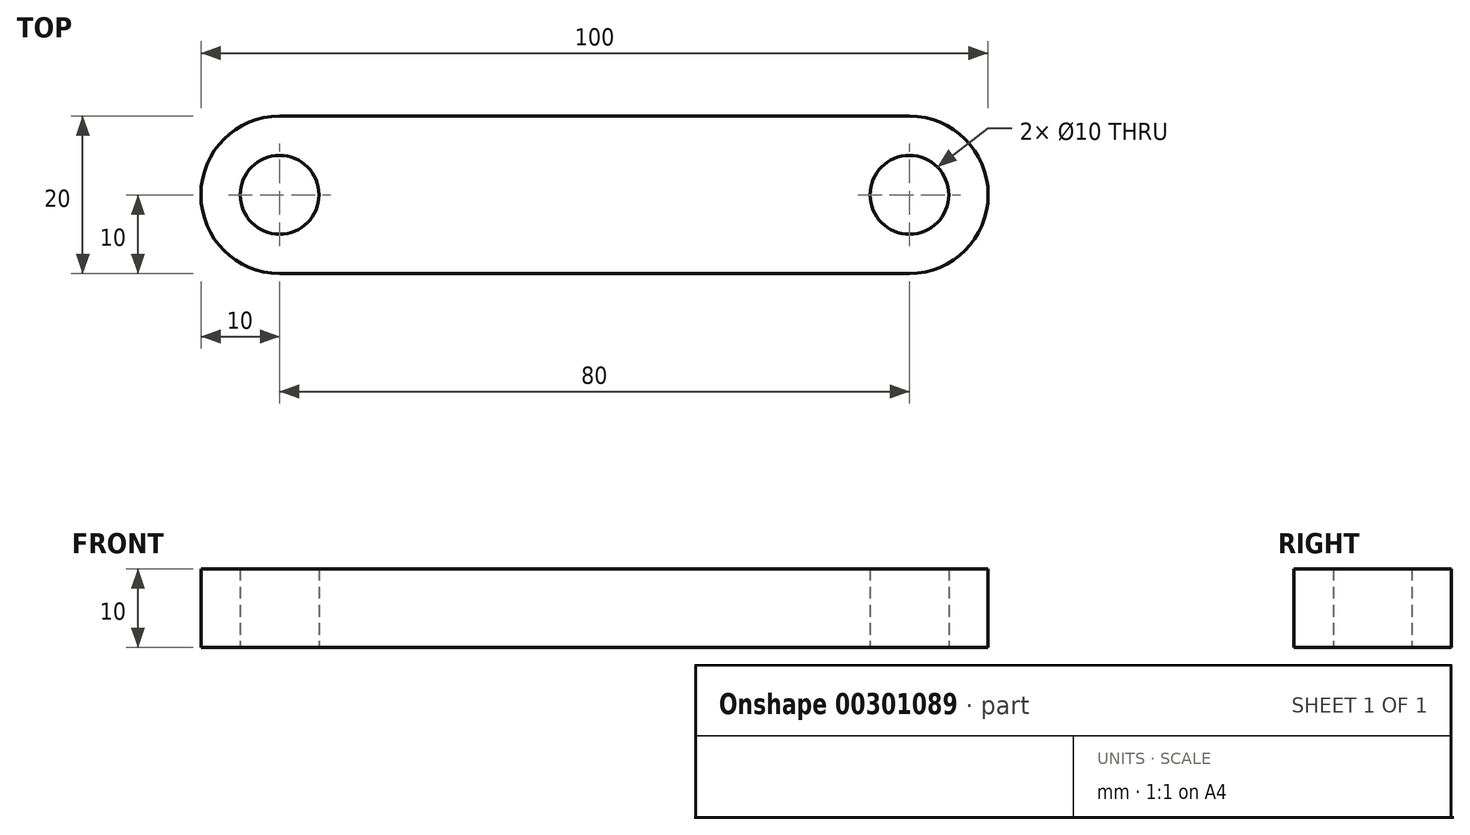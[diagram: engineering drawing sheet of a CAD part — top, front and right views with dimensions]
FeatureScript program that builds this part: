
annotation { "Feature Type Name" : "Feature", "Feature Type Description" : "" }
export const myFeature = defineFeature(function(context is Context, id is Id, definition is map)
    precondition{}
    {
        {
            var Q0;
            Q0=qCreatedBy(makeId("Top.planeOp"),FACE);
            var sketch = newSketch(context, id + "F0", { "sketchPlane" : qUnion([Q0])});
            skArc(sketch, "E0", {"start": v(0, 10) * mm, "mid": v(-10, 0) * mm, "end": v(0, -10) * mm});
            skLineSegment(sketch, "E1", {"start": v(0, -10) * mm, "end": v(80, -10) * mm});
            skLineSegment(sketch, "E2", {"start": v(0, 10) * mm, "end": v(80, 10) * mm});
            skArc(sketch, "E3", {"start": v(80, -10) * mm, "mid": v(90, 0) * mm, "end": v(80, 10) * mm});
            skCircle(sketch, "E4", {"center": v(0, 0) * mm, "radius": 5 * mm});
            skCircle(sketch, "E5", {"center": v(80, 0) * mm, "radius": 5 * mm});
            skSolve(sketch);
        }
        {
            var Q0;
            Q0 = qSketchRegion(id + "F0", true);
            extrude(context, id + "F1", {"entities" : qUnion([Q0]), "depth" : 10 * mm});
        }
    });
